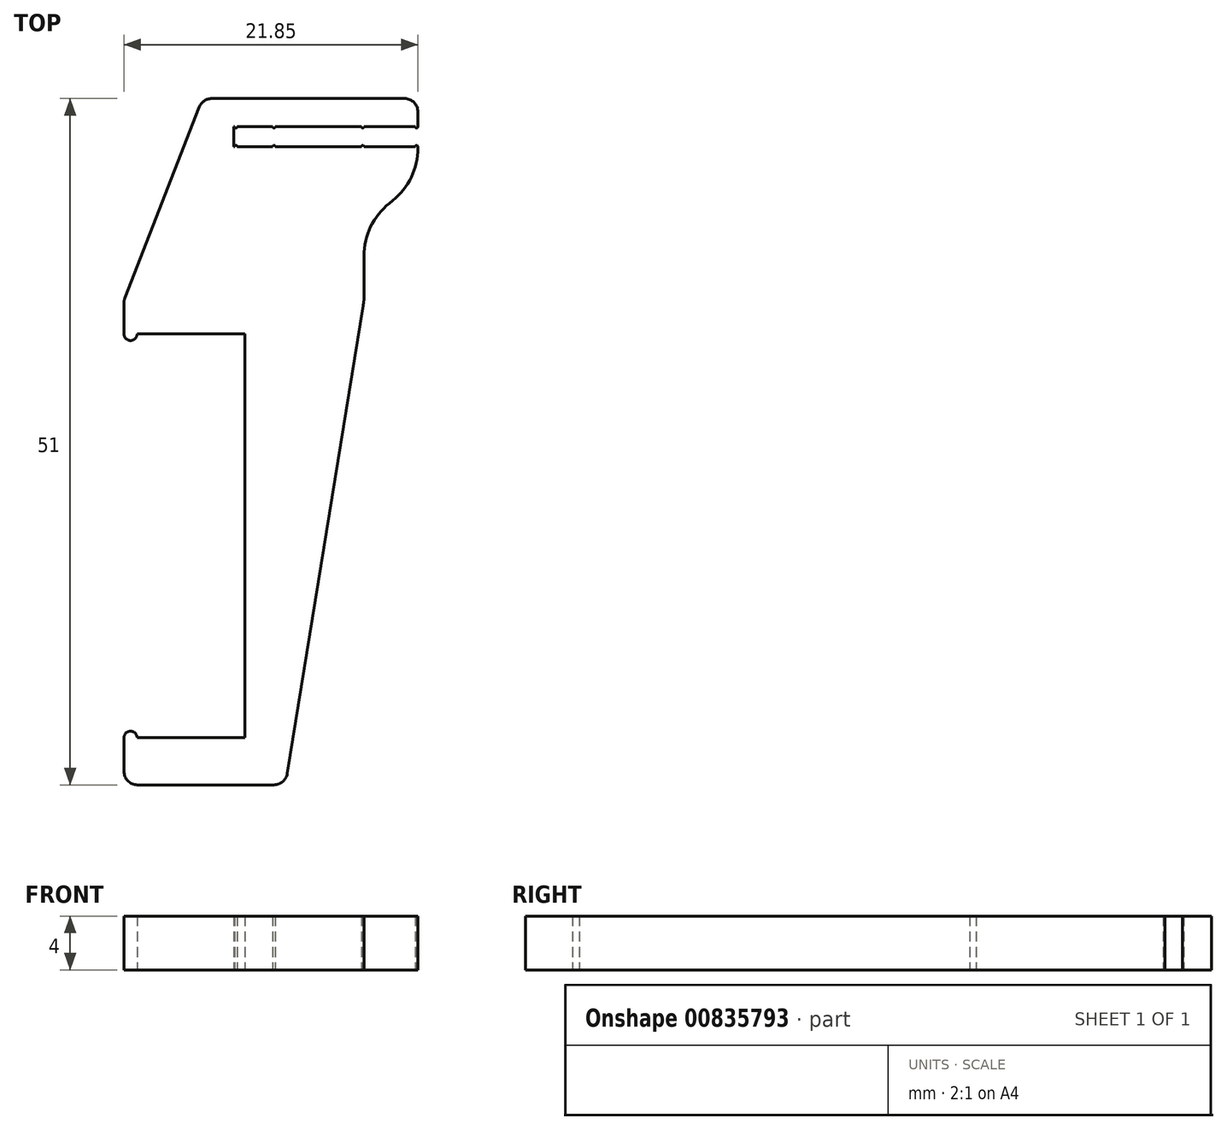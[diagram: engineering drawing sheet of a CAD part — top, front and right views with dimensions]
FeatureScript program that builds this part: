
annotation { "Feature Type Name" : "Feature", "Feature Type Description" : "" }
export const myFeature = defineFeature(function(context is Context, id is Id, definition is map)
    precondition{}
    {
        {
            var Q0;
            Q0=qCreatedBy(makeId("Top.planeOp"),FACE);
            var sketch = newSketch(context, id + "F0", { "sketchPlane" : qUnion([Q0])});
            skLineSegment(sketch, "E0", {"start": v(0, 0) * mm, "end": v(0, -2.5) * mm});
            skLineSegment(sketch, "E1", {"start": v(0, -36) * mm, "end": v(12, -36) * mm});
            skLineSegment(sketch, "E2", {"start": v(5.85, 15) * mm, "end": v(17.85, 15) * mm});
            skLineSegment(sketch, "E3", {"start": v(5.85, 15) * mm, "end": v(0, 0) * mm});
            skLineSegment(sketch, "E4", {"start": v(17.85, 0) * mm, "end": v(12, -36) * mm});
            skLineSegment(sketch, "E5", {"start": v(17.65, 12.91) * mm, "end": v(11.25, 12.91) * mm});
            skLineSegment(sketch, "E6", {"start": v(8.15, 12.91) * mm, "end": v(8.15, 11.41) * mm});
            skLineSegment(sketch, "E7", {"start": v(8.15, 11.41) * mm, "end": v(8.23, 11.41) * mm});
            skLineSegment(sketch, "E8.trimOffspring", {"start": v(17.85, 5.7) * mm, "end": v(17.85, 0) * mm});
            skLineSegment(sketch, "E9", {"start": v(9, -2.5) * mm, "end": v(9, -32.5) * mm});
            skLineSegment(sketch, "E10", {"start": v(9, -32.5) * mm, "end": v(0.98, -32.5) * mm});
            skLineSegment(sketch, "E11", {"start": v(0.98, -2.5) * mm, "end": v(0.98, -32.5) * mm, "construction": true});
            skArc(sketch, "E12", {"start": v(0.98, -2.5) * mm, "mid": v(0.49, -2.99) * mm, "end": v(0, -2.5) * mm});
            skArc(sketch, "E13", {"start": v(0, -32.5) * mm, "mid": v(0.49, -32) * mm, "end": v(0.98, -32.5) * mm});
            skLineSegment(sketch, "E14", {"start": v(17.65, 12.91) * mm, "end": v(17.65, 11.41) * mm, "construction": true});
            skArc(sketch, "E15", {"start": v(17.85, 12.91) * mm, "mid": v(17.75, 12.81) * mm, "end": v(17.65, 12.91) * mm});
            skArc(sketch, "E16", {"start": v(17.65, 11.41) * mm, "mid": v(17.75, 11.51) * mm, "end": v(17.85, 11.41) * mm});
            skPoint(sketch, "E17.start.orphan", {"position": v(6, 0) * mm});
            skPoint(sketch, "E18.end.orphan", {"position": v(12, 0) * mm});
            skLineSegment(sketch, "E19.trimOffspring", {"start": v(0, -32.5) * mm, "end": v(0, -36) * mm});
            skLineSegment(sketch, "E20.trimOffspring", {"start": v(0.98, -2.5) * mm, "end": v(9, -2.5) * mm});
            skPoint(sketch, "E21.start.orphan", {"position": v(0, -2.5) * mm});
            skArc(sketch, "E22", {"start": v(11.25, 12.91) * mm, "mid": v(11.15, 12.81) * mm, "end": v(11.05, 12.91) * mm});
            skLineSegment(sketch, "E23", {"start": v(11.15, 12.91) * mm, "end": v(11.15, 11.41) * mm, "construction": true});
            skArc(sketch, "E24", {"start": v(11.25, 11.41) * mm, "mid": v(11.15, 11.51) * mm, "end": v(11.05, 11.41) * mm});
            skLineSegment(sketch, "E25.trimOffspring", {"start": v(11.05, 12.91) * mm, "end": v(8.43, 12.91) * mm});
            skLineSegment(sketch, "E26.trimOffspring", {"start": v(11.25, 11.41) * mm, "end": v(17.65, 11.41) * mm});
            skLineSegment(sketch, "E27", {"start": v(8.33, 12.91) * mm, "end": v(8.33, 11.41) * mm, "construction": true});
            skArc(sketch, "E28", {"start": v(8.43, 12.91) * mm, "mid": v(8.33, 12.81) * mm, "end": v(8.23, 12.91) * mm});
            skArc(sketch, "E29", {"start": v(8.43, 11.41) * mm, "mid": v(8.33, 11.51) * mm, "end": v(8.23, 11.41) * mm});
            skLineSegment(sketch, "E30.trimOffspring", {"start": v(8.43, 11.41) * mm, "end": v(11.05, 11.41) * mm});
            skLineSegment(sketch, "E31.trimOffspring", {"start": v(8.23, 12.91) * mm, "end": v(8.15, 12.91) * mm});
            skLineSegment(sketch, "E32", {"start": v(17.85, 15) * mm, "end": v(21.85, 15) * mm});
            skLineSegment(sketch, "E33", {"start": v(21.85, 15) * mm, "end": v(21.85, 12.91) * mm});
            skLineSegment(sketch, "E34", {"start": v(17.85, 12.91) * mm, "end": v(21.65, 12.91) * mm});
            skLineSegment(sketch, "E35", {"start": v(21.65, 11.41) * mm, "end": v(17.85, 11.41) * mm});
            skLineSegment(sketch, "E36", {"start": v(21.85, 8.92) * mm, "end": v(17.85, 5.7) * mm});
            skPoint(sketch, "E37.start.orphan", {"position": v(21.85, 0) * mm});
            skLineSegment(sketch, "E38.trimOffspring", {"start": v(21.85, 11.41) * mm, "end": v(21.85, 8.92) * mm});
            skLineSegment(sketch, "E39", {"start": v(21.65, 12.91) * mm, "end": v(21.65, 11.41) * mm, "construction": true});
            skLineSegment(sketch, "E40", {"start": v(21.85, 12.91) * mm, "end": v(21.85, 11.41) * mm, "construction": true});
            skArc(sketch, "E41", {"start": v(21.85, 12.91) * mm, "mid": v(21.75, 12.81) * mm, "end": v(21.65, 12.91) * mm});
            skArc(sketch, "E42", {"start": v(21.85, 11.41) * mm, "mid": v(21.75, 11.51) * mm, "end": v(21.65, 11.41) * mm});
            skSolve(sketch);
        }
        {
            var Q0;
            {var subQ8=sQuery(id+"F0.wireOp",EDGE,"E0");Q0=makeQuery(id+"F0.imprint","IMPRINT",FACE,{"disambiguationData":[TD([[makeQuery(id+"F0.imprint","IMPRINT",EDGE,{"derivedFrom":subQ8}),1.0]])]});}
            extrude(context, id + "F1", {"entities" : qUnion([Q0]), "depth" : 4 * mm, "offsetDistance" : 25 * mm});
        }
        {
            var Q0;
            Q0=makeQuery(id+"F1.opExtrude","SWEPT_EDGE",EDGE,{"disambiguationData":[OSD([sQuery(id+"F0.wireOp",EDGE,"E36"),sQuery(id+"F0.wireOp",EDGE,"E38.trimOffspring")])]});
            var Q1;
            Q1=makeQuery(id+"F1.opExtrude","SWEPT_EDGE",EDGE,{"disambiguationData":[OSD([sQuery(id+"F0.wireOp",EDGE,"E8.trimOffspring"),sQuery(id+"F0.wireOp",EDGE,"E36")])]});
            var Q2;
            Q2=makeQuery(id+"F1.opExtrude","SWEPT_EDGE",EDGE,{"disambiguationData":[OSD([sQuery(id+"F0.wireOp",EDGE,"E4"),sQuery(id+"F0.wireOp",EDGE,"E8.trimOffspring")])]});
            fillet(context, id + "F2", {"entities" : qUnion([Q0, Q1, Q2]), "radius" : 5 * mm, "tangentPropagation" : true, "allowEdgeOverflow" : false});
        }
        {
            var Q0;
            Q0=makeQuery(id+"F1.opExtrude","SWEPT_EDGE",EDGE,{"disambiguationData":[OSD([sQuery(id+"F0.wireOp",EDGE,"E32"),sQuery(id+"F0.wireOp",EDGE,"E33")])]});
            var Q1;
            Q1=makeQuery(id+"F1.opExtrude","SWEPT_EDGE",EDGE,{"disambiguationData":[OSD([sQuery(id+"F0.wireOp",EDGE,"E2"),sQuery(id+"F0.wireOp",EDGE,"E3")])]});
            var Q2;
            Q2=makeQuery(id+"F1.opExtrude","SWEPT_EDGE",EDGE,{"disambiguationData":[OSD([sQuery(id+"F0.wireOp",EDGE,"E0"),sQuery(id+"F0.wireOp",EDGE,"E3")])]});
            var Q3;
            Q3=makeQuery(id+"F1.opExtrude","SWEPT_EDGE",EDGE,{"disambiguationData":[OSD([sQuery(id+"F0.wireOp",EDGE,"E1"),sQuery(id+"F0.wireOp",EDGE,"E4")])]});
            var Q4;
            Q4=makeQuery(id+"F1.opExtrude","SWEPT_EDGE",EDGE,{"disambiguationData":[OSD([sQuery(id+"F0.wireOp",EDGE,"E1"),sQuery(id+"F0.wireOp",EDGE,"E19.trimOffspring")])]});
            fillet(context, id + "F3", {"entities" : qUnion([Q0, Q1, Q2, Q3, Q4]), "radius" : 1 * mm, "tangentPropagation" : true, "allowEdgeOverflow" : false});
        }
    });
